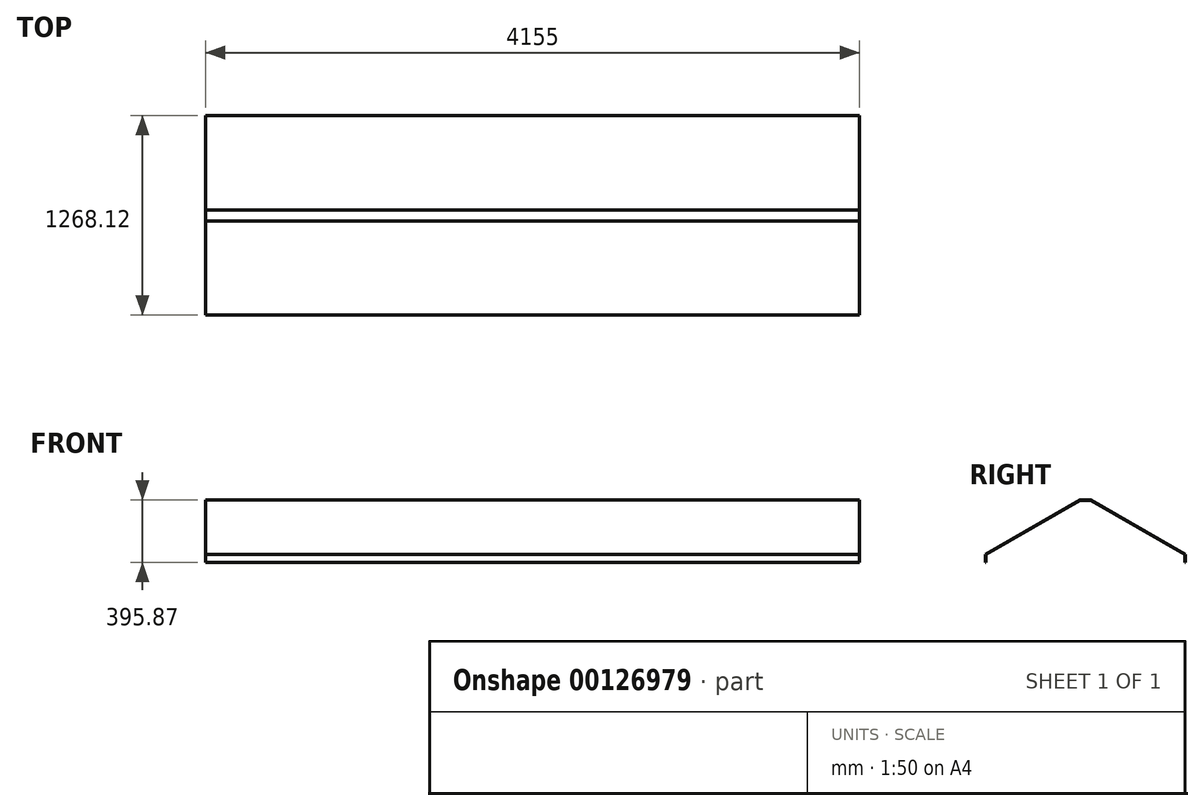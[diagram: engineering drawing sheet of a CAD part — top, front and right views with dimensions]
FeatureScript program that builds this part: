
annotation { "Feature Type Name" : "Feature", "Feature Type Description" : "" }
export const myFeature = defineFeature(function(context is Context, id is Id, definition is map)
    precondition{}
    {
        {
            var Q0;
            Q0=qCreatedBy(makeId("Right.planeOp"),FACE);
            var sketch = newSketch(context, id + "F0", { "sketchPlane" : qUnion([Q0])});
            skLineSegment(sketch, "E0", {"start": v(0, 0) * mm, "end": v(70, 0) * mm});
            skLineSegment(sketch, "E1", {"start": v(0, 0) * mm, "end": v(-597.56, -345) * mm});
            skLineSegment(sketch, "E2", {"start": v(70, 0) * mm, "end": v(667.56, -345) * mm});
            skLineSegment(sketch, "E3", {"start": v(-597.06, -345.87) * mm, "end": v(0, -1.15) * mm});
            skLineSegment(sketch, "E4", {"start": v(667.06, -345.87) * mm, "end": v(70, -1.15) * mm});
            skLineSegment(sketch, "E5", {"start": v(0, -1.15) * mm, "end": v(70, -1.15) * mm});
            skLineSegment(sketch, "E6", {"start": v(-597.56, -345) * mm, "end": v(-599.06, -345.87) * mm});
            skPoint(sketch, "E7.endSnap0", {"position": v(-599.06, -345.87) * mm});
            skLineSegment(sketch, "E8", {"start": v(-597.06, -345.87) * mm, "end": v(-597.06, -395.87) * mm});
            skLineSegment(sketch, "E9", {"start": v(-599.06, -345.87) * mm, "end": v(-599.06, -395.87) * mm});
            skLineSegment(sketch, "E10", {"start": v(-599.06, -395.87) * mm, "end": v(-597.06, -395.87) * mm});
            skPoint(sketch, "E11.orphan", {"position": v(-600.56, -346.73) * mm});
            skPoint(sketch, "E12.orphan", {"position": v(-600.56, -345.87) * mm});
            skLineSegment(sketch, "E13", {"start": v(667.56, -345) * mm, "end": v(669.06, -345.87) * mm});
            skLineSegment(sketch, "E14", {"start": v(667.06, -345.87) * mm, "end": v(667.06, -395.87) * mm});
            skLineSegment(sketch, "E15", {"start": v(669.06, -345.87) * mm, "end": v(669.06, -395.87) * mm});
            skLineSegment(sketch, "E16", {"start": v(667.06, -395.87) * mm, "end": v(669.06, -395.87) * mm});
            skSolve(sketch);
        }
        {
            var Q0;
            Q0=makeQuery(id+"F0.imprint","IMPRINT",FACE,{"disambiguationData":[TD([[makeQuery(id+"F0.imprint","IMPRINT",EDGE,{"derivedFrom":sQuery(id+"F0.wireOp",EDGE,"E0")}),-1.0]])]});
            extrude(context, id + "F1", {"entities" : qUnion([Q0]), "depth" : 4155 * mm});
        }
    });
